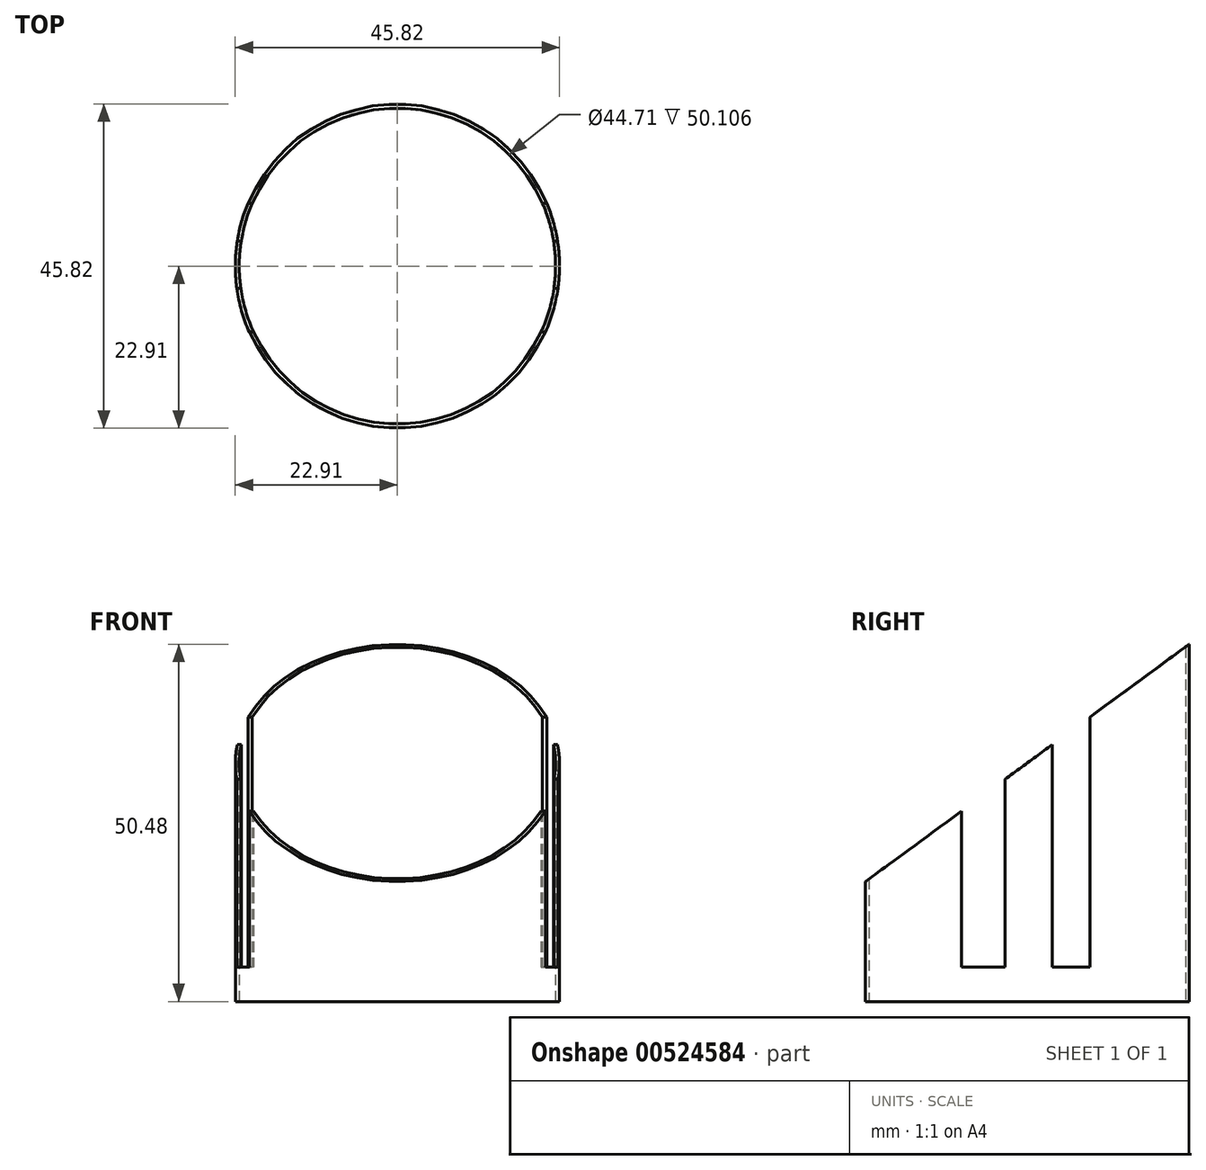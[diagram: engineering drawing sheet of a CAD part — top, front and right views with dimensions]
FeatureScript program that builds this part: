
annotation { "Feature Type Name" : "Feature", "Feature Type Description" : "" }
export const myFeature = defineFeature(function(context is Context, id is Id, definition is map)
    precondition{}
    {
        {
            var Q0;
            Q0=qCreatedBy(makeId("Top.planeOp"),FACE);
            var sketch = newSketch(context, id + "F0", { "sketchPlane" : qUnion([Q0])});
            skCircle(sketch, "E0", {"center": v(0, 0) * mm, "radius": 22.9 * mm});
            skSolve(sketch);
        }
        {
            var Q0;
            Q0 = qSketchRegion(id + "F0", true);
            extrude(context, id + "F1", {"entities" : qUnion([Q0]), "depth" : 51.1 * mm, "offsetDistance" : 25 * mm});
        }
        {
            var Q0;
            Q0=qCreatedBy(makeId("Right.planeOp"),FACE);
            cPlane(context, id + "F2", {"entities" : qUnion([Q0]), "cplaneType" : CPlaneType.OFFSET, "offset" : 32.2 * mm, "oppositeDirection" : true, "width" : 150 * mm, "height" : 150 * mm});
        }
        {
            var Q0;
            Q0=qCreatedBy(id+"F2.planeOp",FACE);
            var sketch = newSketch(context, id + "F3", { "sketchPlane" : qUnion([Q0])});
            skLineSegment(sketch, "E1", {"start": v(31.37, 56.67) * mm, "end": v(-46.02, 0) * mm});
            skLineSegment(sketch, "E2", {"start": v(-46.02, 0) * mm, "end": v(-37.55, 54.17) * mm});
            skLineSegment(sketch, "E3", {"start": v(-37.55, 54.17) * mm, "end": v(31.37, 56.67) * mm});
            skSolve(sketch);
        }
        {
            var Q0;
            Q0 = qSketchRegion(id + "F3", true);
            extrude(context, id + "F4", {"entities" : qUnion([Q0]), "operationType" : NewBodyOperationType.REMOVE, "depth" : 106.8 * mm, "offsetDistance" : 25 * mm});
        }
        {
            var Q0;
            Q0=qCreatedBy(makeId("Top.planeOp"),FACE);
            var sketch = newSketch(context, id + "F5", { "sketchPlane" : qUnion([Q0])});
            skCircle(sketch, "E4", {"center": v(0, 0) * mm, "radius": 22.36 * mm});
            skCircle(sketch, "E5", {"center": v(0, 0) * mm, "radius": 21 * mm});
            skSolve(sketch);
        }
        {
            var Q0;
            Q0 = qSketchRegion(id + "F5", true);
            extrude(context, id + "F6", {"entities" : qUnion([Q0]), "operationType" : NewBodyOperationType.REMOVE, "depth" : 54.8 * mm, "offsetDistance" : 25 * mm});
        }
        {
            var Q0;
            Q0=qCreatedBy(makeId("Top.planeOp"),FACE);
            var sketch = newSketch(context, id + "F7", { "sketchPlane" : qUnion([Q0])});
            skCircle(sketch, "E6", {"center": v(0, 0) * mm, "radius": 21.54 * mm});
            skSolve(sketch);
        }
        {
            var Q0;
            Q0 = qSketchRegion(id + "F7", true);
            extrude(context, id + "F8", {"entities" : qUnion([Q0]), "operationType" : NewBodyOperationType.REMOVE, "depth" : 64.2 * mm, "offsetDistance" : 25 * mm});
        }
        {
            var Q0;
            Q0=qCreatedBy(id+"F2.planeOp",FACE);
            var sketch = newSketch(context, id + "F9", { "sketchPlane" : qUnion([Q0])});
            skLineSegment(sketch, "E7.bottom", {"start": v(-9.32, 38.1) * mm, "end": v(-3.17, 38.1) * mm});
            skLineSegment(sketch, "E7.top", {"start": v(-9.32, 4.87) * mm, "end": v(-3.17, 4.87) * mm});
            skLineSegment(sketch, "E7.left", {"start": v(-9.32, 38.1) * mm, "end": v(-9.32, 4.87) * mm});
            skLineSegment(sketch, "E7.right", {"start": v(-3.17, 38.1) * mm, "end": v(-3.17, 4.87) * mm});
            skLineSegment(sketch, "E8.bottom", {"start": v(3.54, 42.72) * mm, "end": v(8.87, 42.72) * mm});
            skLineSegment(sketch, "E8.top", {"start": v(3.54, 4.87) * mm, "end": v(8.87, 4.87) * mm});
            skLineSegment(sketch, "E8.left", {"start": v(3.54, 42.72) * mm, "end": v(3.54, 4.87) * mm});
            skLineSegment(sketch, "E8.right", {"start": v(8.87, 42.72) * mm, "end": v(8.87, 4.87) * mm});
            skSolve(sketch);
        }
        {
            var Q0;
            Q0 = qSketchRegion(id + "F9", true);
            extrude(context, id + "F10", {"entities" : qUnion([Q0]), "operationType" : NewBodyOperationType.REMOVE, "depth" : 98.8 * mm, "offsetDistance" : 25 * mm});
        }
        {
            var Q0;
            Q0 = qSketchRegion(id + "F9", true);
            extrude(context, id + "F11", {"entities" : qUnion([Q0]), "operationType" : NewBodyOperationType.REMOVE, "depth" : 96.1 * mm, "offsetDistance" : 25 * mm});
        }
    });
